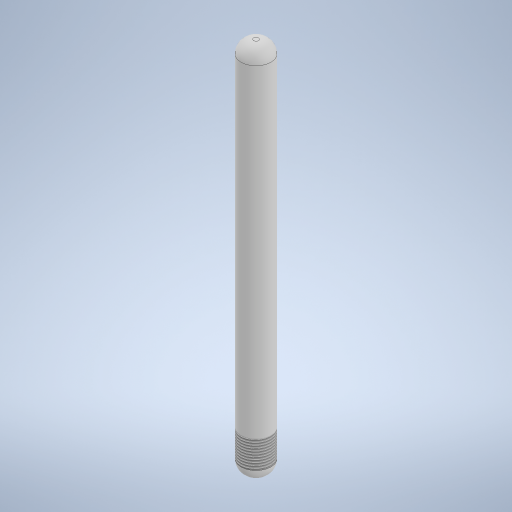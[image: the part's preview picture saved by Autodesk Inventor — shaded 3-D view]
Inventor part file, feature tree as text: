
AUTODESK INVENTOR PART (.ipt)
format: ipt  version: 2023.2 (Build 272271030, 271C)  size: 244,224 bytes
history: native  units: mm
features: fillet x2, extrude x1, thread x1, sketch x1
ambient origin geometry x8: Origin, YZ Plane, XZ Plane, XY Plane, X Axis, Y Axis, Z Axis, Center Point
bodies: Solid1 (feature_tree)
feature tree (5):
  extrude  "Extrusion1"  Depth=150.0mm TaperAngle=0.0deg
  fillet  "Fillet1"  Radius=5.0mm
  fillet  "Fillet2"  Radius=5.0mm
  thread  "Thread1"  [1 undecoded]
  sketch  "Sketch1"  dims[d0=12.0mm d1=150.0mm d2=0.0mm d3=5.0mm d4=5.0mm d5=11.0mm d6=0.0mm]
note: 1 required parameter value undecoded (feature->parameter linkage not recoverable at this tier; creation-order binding heuristic only, values carry confidence <= 0.55)
